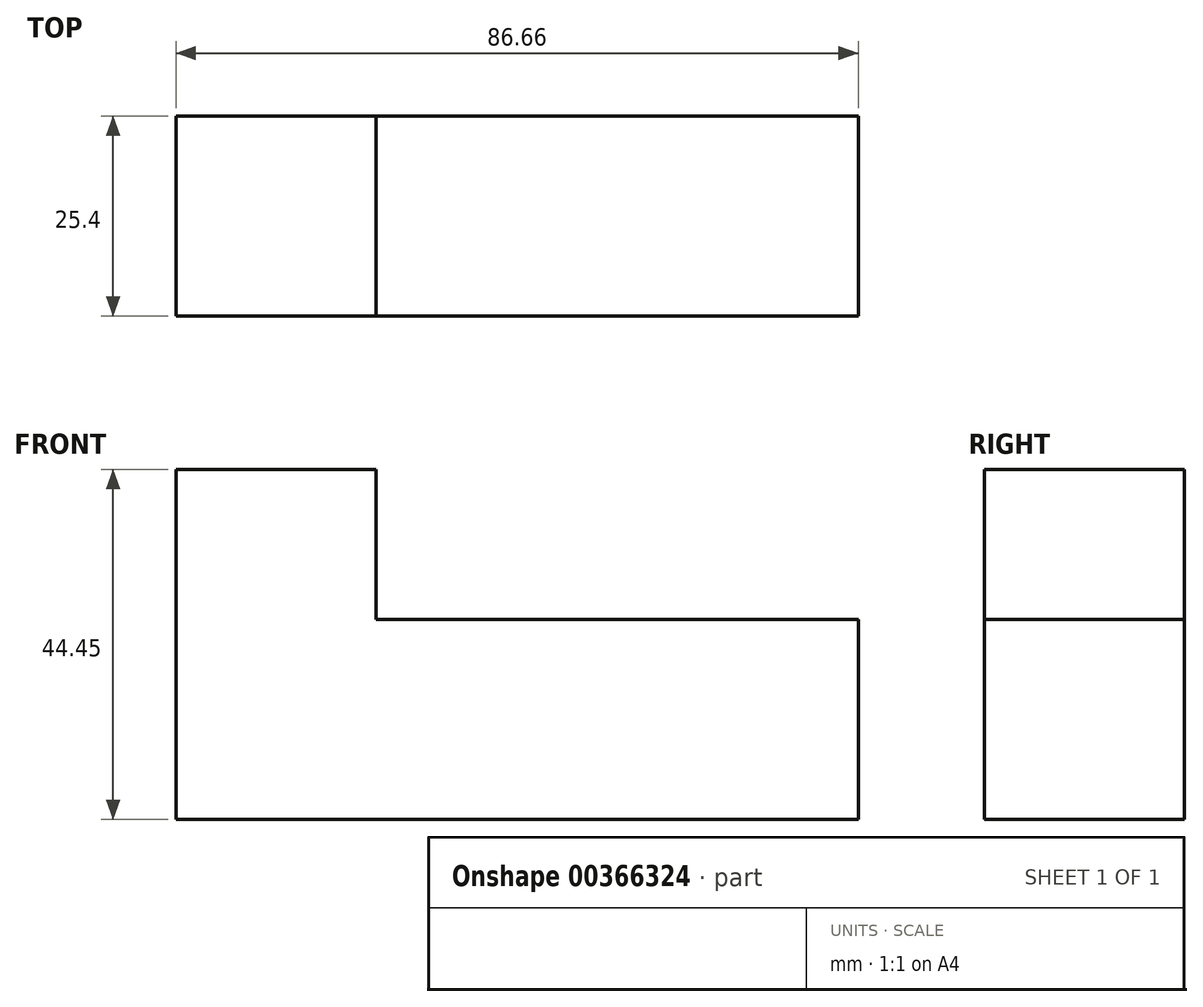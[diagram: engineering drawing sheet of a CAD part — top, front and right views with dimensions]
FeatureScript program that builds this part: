
annotation { "Feature Type Name" : "Feature", "Feature Type Description" : "" }
export const myFeature = defineFeature(function(context is Context, id is Id, definition is map)
    precondition{}
    {
        {
            var Q0;
            Q0=qCreatedBy(makeId("Front.planeOp"),FACE);
            var sketch = newSketch(context, id + "F0", { "sketchPlane" : qUnion([Q0])});
            skLineSegment(sketch, "E0", {"start": v(0, 0) * mm, "end": v(86.66, 0) * mm});
            skLineSegment(sketch, "E1", {"start": v(86.66, 0) * mm, "end": v(86.66, 25.4) * mm});
            skLineSegment(sketch, "E2", {"start": v(86.66, 25.4) * mm, "end": v(25.4, 25.4) * mm});
            skLineSegment(sketch, "E3", {"start": v(25.4, 25.4) * mm, "end": v(25.4, 44.45) * mm});
            skLineSegment(sketch, "E4", {"start": v(25.4, 44.45) * mm, "end": v(0, 44.45) * mm});
            skLineSegment(sketch, "E5", {"start": v(0, 44.45) * mm, "end": v(0, 0) * mm});
            skSolve(sketch);
        }
        {
            var Q0;
            Q0=makeQuery(id+"F0.imprint","IMPRINT",FACE,{"disambiguationData":[TD([[makeQuery(id+"F0.imprint","IMPRINT",EDGE,{"derivedFrom":sQuery(id+"F0.wireOp",EDGE,"E0")}),1.0]])]});
            extrude(context, id + "F1", {"entities" : qUnion([Q0]), "depth" : 25.4 * mm});
        }
    });
